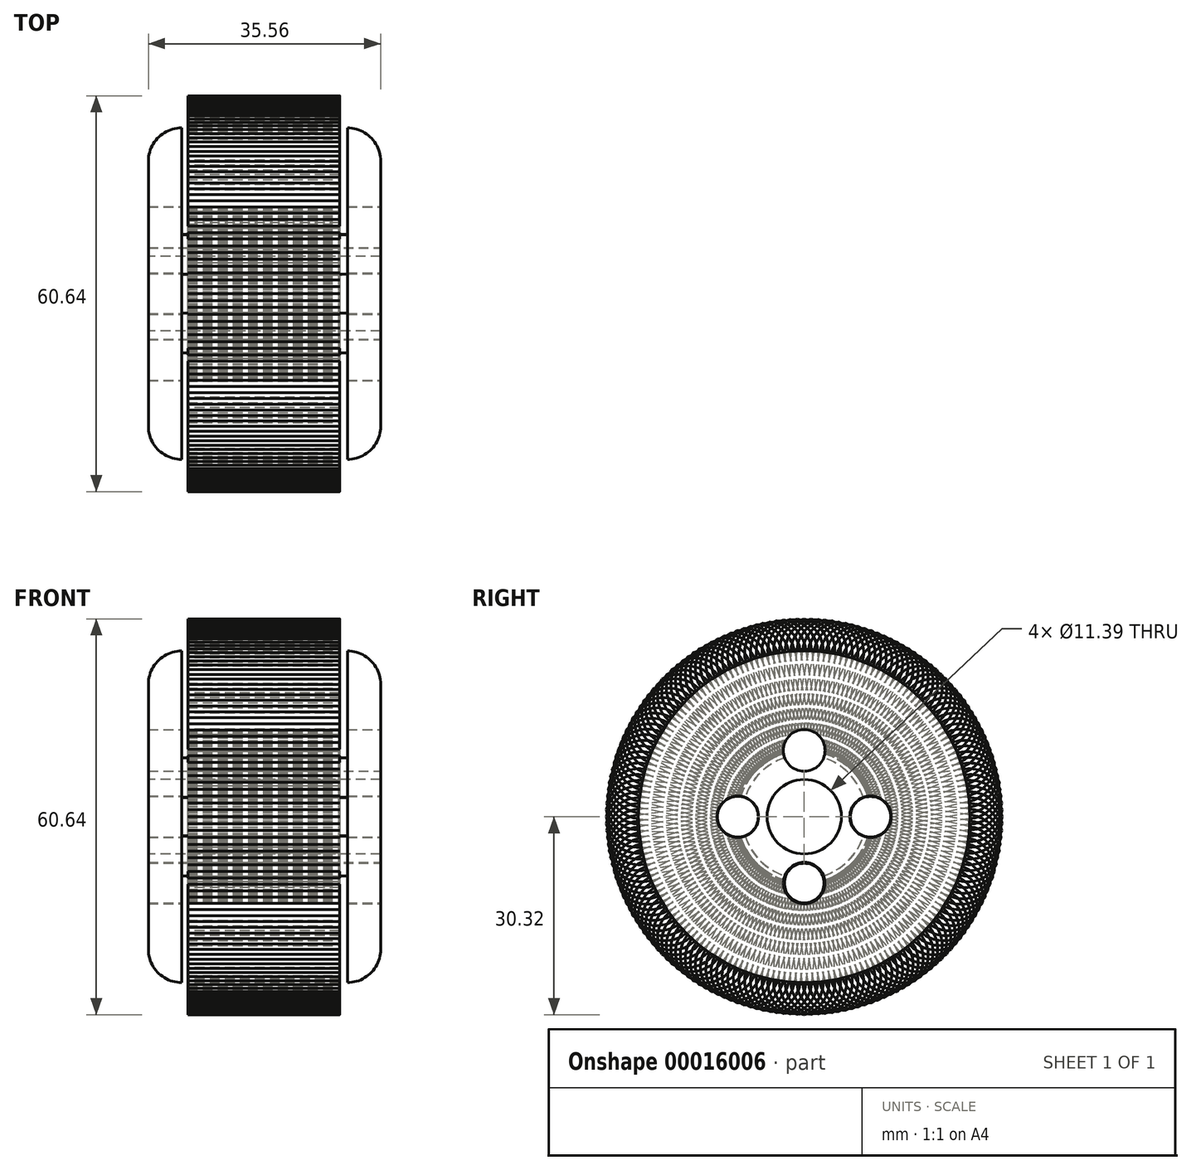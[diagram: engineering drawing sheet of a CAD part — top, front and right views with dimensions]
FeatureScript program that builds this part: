
annotation { "Feature Type Name" : "Feature", "Feature Type Description" : "" }
export const myFeature = defineFeature(function(context is Context, id is Id, definition is map)
    precondition{}
    {
        {
            var Q0;
            Q0=qCreatedBy(makeId("Right.planeOp"),FACE);
            var sketch = newSketch(context, id + "F0", { "sketchPlane" : qUnion([Q0])});
            skCircle(sketch, "E0", {"center": v(0, 0) * mm, "radius": 25.4 * mm});
            skSolve(sketch);
        }
        {
            var Q0;
            Q0 = qSketchRegion(id + "F0", true);
            extrude(context, id + "F1", {"entities" : qUnion([Q0]), "depth" : 5.08 * mm});
        }
        {
            var Q0;
            Q0=makeQuery(id+"F1.opExtrude","CAP_FACE",FACE,{"disambiguationData":[OSD([sQuery(id+"F0.wireOp",EDGE,"E0")])],"isStart":false});
            var sketch = newSketch(context, id + "F2", { "sketchPlane" : qUnion([Q0])});
            skCircle(sketch, "E1", {"center": v(0, 0) * mm, "radius": 9.52 * mm});
            skSolve(sketch);
        }
        {
            var Q0;
            Q0 = qSketchRegion(id + "F2", true);
            extrude(context, id + "F3", {"entities" : qUnion([Q0]), "operationType" : NewBodyOperationType.ADD, "depth" : 25.4 * mm});
        }
        {
            var Q0;
            Q0=makeQuery(id+"F3.opExtrude","CAP_FACE",FACE,{"disambiguationData":[OSD([sQuery(id+"F2.wireOp",EDGE,"E1")])],"isStart":false});
            var sketch = newSketch(context, id + "F4", { "sketchPlane" : qUnion([Q0])});
            skCircle(sketch, "E2", {"center": v(0, 0) * mm, "radius": 25.4 * mm});
            skSolve(sketch);
        }
        {
            var Q0;
            Q0 = qSketchRegion(id + "F4", true);
            extrude(context, id + "F5", {"entities" : qUnion([Q0]), "operationType" : NewBodyOperationType.ADD, "depth" : 5.08 * mm});
        }
        {
            var Q0;
            Q0=qCreatedBy(makeId("Front.planeOp"),FACE);
            cPlane(context, id + "F6", {"entities" : qUnion([Q0]), "cplaneType" : CPlaneType.OFFSET, "offset" : 25.4 * mm, "width" : 152.4 * mm, "height" : 152.4 * mm});
        }
        {
            var Q0;
            Q0=qCreatedBy(id+"F6.planeOp",FACE);
            var sketch = newSketch(context, id + "F7", { "sketchPlane" : qUnion([Q0])});
            skLineSegment(sketch, "E3", {"start": v(6.03, 0) * mm, "end": v(6.03, 3.81) * mm});
            skLineSegment(sketch, "E4", {"start": v(6.03, 0) * mm, "end": v(6.03, -3.81) * mm});
            skLineSegment(sketch, "E5", {"start": v(29.3, 0) * mm, "end": v(29.3, 3.8) * mm});
            skLineSegment(sketch, "E6", {"start": v(29.3, 0) * mm, "end": v(29.3, -3.81) * mm});
            skLineSegment(sketch, "E7", {"start": v(6.03, 3.81) * mm, "end": v(29.3, 3.81) * mm});
            skLineSegment(sketch, "E8", {"start": v(6.03, -3.81) * mm, "end": v(29.3, -3.81) * mm});
            skSolve(sketch);
        }
        {
            var Q0;
            Q0 = qSketchRegion(id + "F7", true);
            extrude(context, id + "F8", {"entities" : qUnion([Q0]), "operationType" : NewBodyOperationType.ADD, "depth" : 5.08 * mm, "hasSecondDirection" : true, "secondDirectionOppositeDirection" : true, "secondDirectionDepth" : 15.21 * mm});
        }
        {
            var Q0;
            Q0=makeQuery(id+"F8.opExtrude","CAP_EDGE",EDGE,{"disambiguationData":[OSD([sQuery(id+"F7.wireOp",EDGE,"E7")])],"isStart":false});
            var Q1;
            Q1=makeQuery(id+"F8.opExtrude","CAP_EDGE",EDGE,{"disambiguationData":[OSD([sQuery(id+"F7.wireOp",EDGE,"E8")])],"isStart":false});
            fillet(context, id + "F9", {"entities" : qUnion([Q0, Q1]), "radius" : 5.08 * mm, "tangentPropagation" : true, "allowEdgeOverflow" : false});
        }
        {
            var Q0;
            Q0=makeQuery(id+"F8.opExtrude","SWEPT_BODY",BODY,{"disambiguationData":[OSD([sQuery(id+"F7.wireOp",EDGE,"E3"),sQuery(id+"F7.wireOp",EDGE,"E4"),sQuery(id+"F7.wireOp",EDGE,"E5"),sQuery(id+"F7.wireOp",EDGE,"E6"),sQuery(id+"F7.wireOp",EDGE,"E7"),sQuery(id+"F7.wireOp",EDGE,"E8")])]});
            var Q1;
            Q1=makeQuery(id+"F5.opExtrude","CAP_EDGE",EDGE,{"disambiguationData":[OSD([sQuery(id+"F4.wireOp",EDGE,"E2")])],"isStart":false});
            circularPattern(context, id + "F10", {"entities" : qUnion([Q0]), "axis" : qUnion([Q1]), "angle" : 2 * degree, "instanceCount" : 200});
        }
        {
            var Q0;
            Q0=makeQuery(id+"F5.opExtrude","CAP_EDGE",EDGE,{"disambiguationData":[OSD([sQuery(id+"F4.wireOp",EDGE,"E2")])],"isStart":false});
            var Q1;
            Q1=makeQuery(id+"F1.opExtrude","CAP_EDGE",EDGE,{"disambiguationData":[OSD([sQuery(id+"F0.wireOp",EDGE,"E0")])],"isStart":true});
            fillet(context, id + "F11", {"entities" : qUnion([Q0, Q1]), "radius" : 5.08 * mm, "tangentPropagation" : true, "allowEdgeOverflow" : false});
        }
        {
            var Q0;
            Q0=makeQuery(id+"F5.opExtrude","CAP_FACE",FACE,{"disambiguationData":[OSD([sQuery(id+"F4.wireOp",EDGE,"E2")])],"isStart":false});
            var sketch = newSketch(context, id + "F12", { "sketchPlane" : qUnion([Q0])});
            skCircle(sketch, "E9", {"center": v(0, 10.16) * mm, "radius": 3.18 * mm});
            skSolve(sketch);
        }
        {
            var Q0;
            Q0 = qSketchRegion(id + "F12", true);
            extrude(context, id + "F13", {"entities" : qUnion([Q0]), "operationType" : NewBodyOperationType.REMOVE, "oppositeDirection" : true, "depth" : 58.7 * mm});
        }
        {
            var Q0;
            Q0=makeQuery(id+"F1.opExtrude","SWEPT_BODY",BODY,{"disambiguationData":[OSD([sQuery(id+"F0.wireOp",EDGE,"E0")])]});
            var Q1;
            {var subQ0=sQuery(id+"F0.wireOp",EDGE,"E0");Q1=makeQuery(id+"F11.opFillet","BLEND_EDGE",EDGE,{"blendedFrom":[makeQuery(id+"F1.opExtrude","CAP_EDGE",EDGE,{"disambiguationData":[OSD([subQ0])],"isStart":true}),makeQuery(id+"F1.opExtrude","CAP_FACE",FACE,{"disambiguationData":[OSD([subQ0])],"isStart":true})],"blendedInto":[makeQuery(id+"F1.opExtrude","CAP_FACE",FACE,{"disambiguationData":[OSD([subQ0])],"isStart":true})]});}
            circularPattern(context, id + "F14", {"entities" : qUnion([Q0]), "axis" : qUnion([Q1]), "angle" : 90 * degree, "instanceCount" : 4});
        }
        {
            var Q0;
            Q0=makeQuery(id+"F5.opExtrude","CAP_FACE",FACE,{"disambiguationData":[OSD([sQuery(id+"F4.wireOp",EDGE,"E2")])],"isStart":false});
            var sketch = newSketch(context, id + "F15", { "sketchPlane" : qUnion([Q0])});
            skCircle(sketch, "E10", {"center": v(0, 10.16) * mm, "radius": 3.2 * mm});
            skCircle(sketch, "E11", {"center": v(-10.16, 0) * mm, "radius": 3.13 * mm});
            skCircle(sketch, "E12", {"center": v(0, -10.16) * mm, "radius": 3.04 * mm});
            skCircle(sketch, "E13", {"center": v(10.16, 0) * mm, "radius": 3.1 * mm});
            skSolve(sketch);
        }
        {
            var Q0;
            Q0 = qSketchRegion(id + "F15", true);
            extrude(context, id + "F16", {"entities" : qUnion([Q0]), "operationType" : NewBodyOperationType.REMOVE, "oppositeDirection" : true, "depth" : 38.76 * mm});
        }
        {
            var Q0;
            Q0=makeQuery(id+"F14.opPattern","COPY",FACE,{"derivedFrom":makeQuery(id+"F1.opExtrude","CAP_FACE",FACE,{"disambiguationData":[OSD([sQuery(id+"F0.wireOp",EDGE,"E0")])],"isStart":true}),"instanceName":"1"});
            var sketch = newSketch(context, id + "F17", { "sketchPlane" : qUnion([Q0])});
            skCircle(sketch, "E14", {"center": v(0, 0) * mm, "radius": 5.7 * mm});
            skSolve(sketch);
        }
        {
            var Q0;
            Q0 = qSketchRegion(id + "F17", true);
            extrude(context, id + "F18", {"entities" : qUnion([Q0]), "operationType" : NewBodyOperationType.REMOVE, "oppositeDirection" : true, "depth" : 40.1 * mm});
        }
    });
